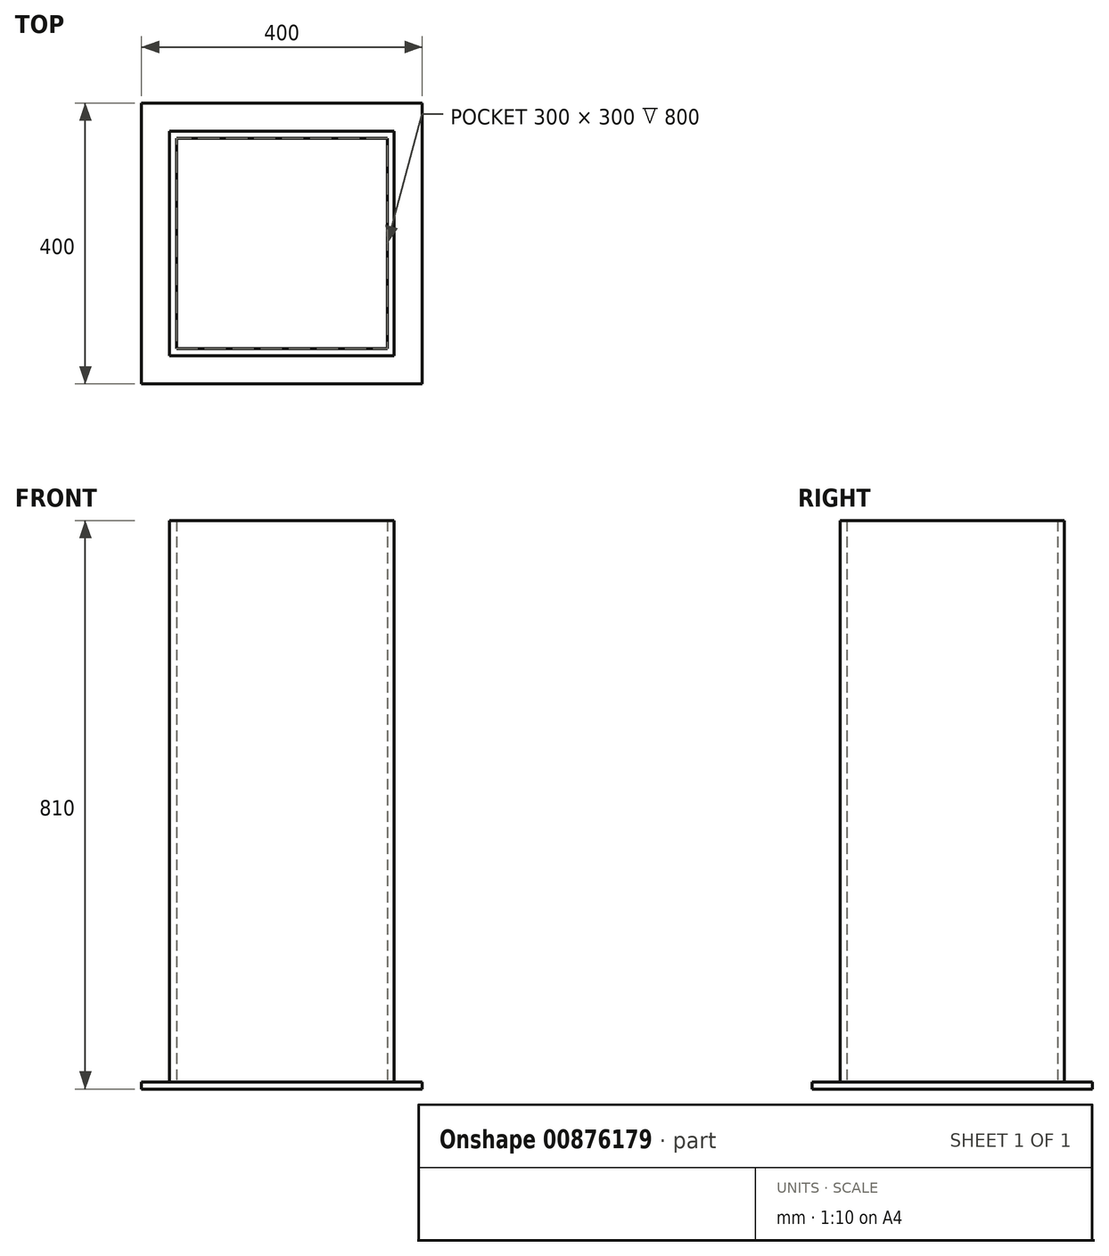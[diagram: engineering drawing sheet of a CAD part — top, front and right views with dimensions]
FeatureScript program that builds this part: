
annotation { "Feature Type Name" : "Feature", "Feature Type Description" : "" }
export const myFeature = defineFeature(function(context is Context, id is Id, definition is map)
    precondition{}
    {
        {
            var Q0;
            Q0=qCreatedBy(makeId("Top.planeOp"),FACE);
            var sketch = newSketch(context, id + "F0", { "sketchPlane" : qUnion([Q0])});
            skLineSegment(sketch, "E0.bottom", {"start": v(150, -150) * mm, "end": v(-150, -150) * mm});
            skLineSegment(sketch, "E0.top", {"start": v(150, 150) * mm, "end": v(-150, 150) * mm});
            skLineSegment(sketch, "E0.left", {"start": v(150, -150) * mm, "end": v(150, 150) * mm});
            skLineSegment(sketch, "E0.right", {"start": v(-150, -150) * mm, "end": v(-150, 150) * mm});
            skPoint(sketch, "E0.middle", {"position": v(0, 0) * mm});
            skLineSegment(sketch, "E1.bottom", {"start": v(160, -160) * mm, "end": v(-160, -160) * mm});
            skLineSegment(sketch, "E1.top", {"start": v(160, 160) * mm, "end": v(-160, 160) * mm});
            skLineSegment(sketch, "E1.left", {"start": v(160, -160) * mm, "end": v(160, 160) * mm});
            skLineSegment(sketch, "E1.right", {"start": v(-160, -160) * mm, "end": v(-160, 160) * mm});
            skSolve(sketch);
        }
        {
            var Q0;
            Q0 = qSketchRegion(id + "F0", true);
            extrude(context, id + "F1", {"entities" : qUnion([Q0]), "depth" : 800 * mm, "offsetDistance" : 25 * mm});
        }
        {
            var Q0;
            Q0=makeQuery(id+"F0.imprint","IMPRINT",FACE,{"disambiguationData":[TD([[makeQuery(id+"F0.imprint","IMPRINT",EDGE,{"derivedFrom":sQuery(id+"F0.wireOp",EDGE,"E0.bottom")}),-1.0]])]});
            var sketch = newSketch(context, id + "F2", { "sketchPlane" : qUnion([Q0])});
            skLineSegment(sketch, "E2.bottom", {"start": v(200, -200) * mm, "end": v(-200, -200) * mm});
            skLineSegment(sketch, "E2.top", {"start": v(200, 200) * mm, "end": v(-200, 200) * mm});
            skLineSegment(sketch, "E2.left", {"start": v(200, -200) * mm, "end": v(200, 200) * mm});
            skLineSegment(sketch, "E2.right", {"start": v(-200, -200) * mm, "end": v(-200, 200) * mm});
            skPoint(sketch, "E2.middle", {"position": v(0, 0) * mm});
            skSolve(sketch);
        }
        {
            var Q0;
            Q0=makeQuery(id+"F2.imprint","IMPRINT",FACE,{"disambiguationData":[TD([[makeQuery(id+"F2.imprint","IMPRINT",EDGE,{"derivedFrom":sQuery(id+"F2.wireOp",EDGE,"E2.bottom")}),-1.0]])]});
            var Q1;
            Q1=makeQuery(id+"F0.imprint","IMPRINT",FACE,{"disambiguationData":[TD([[makeQuery(id+"F0.imprint","IMPRINT",EDGE,{"derivedFrom":sQuery(id+"F0.wireOp",EDGE,"E0.bottom")}),-1.0]])]});
            extrude(context, id + "F3", {"entities" : qUnion([Q0, Q1]), "operationType" : NewBodyOperationType.ADD, "oppositeDirection" : true, "depth" : 10 * mm, "offsetDistance" : 25 * mm});
        }
    });
